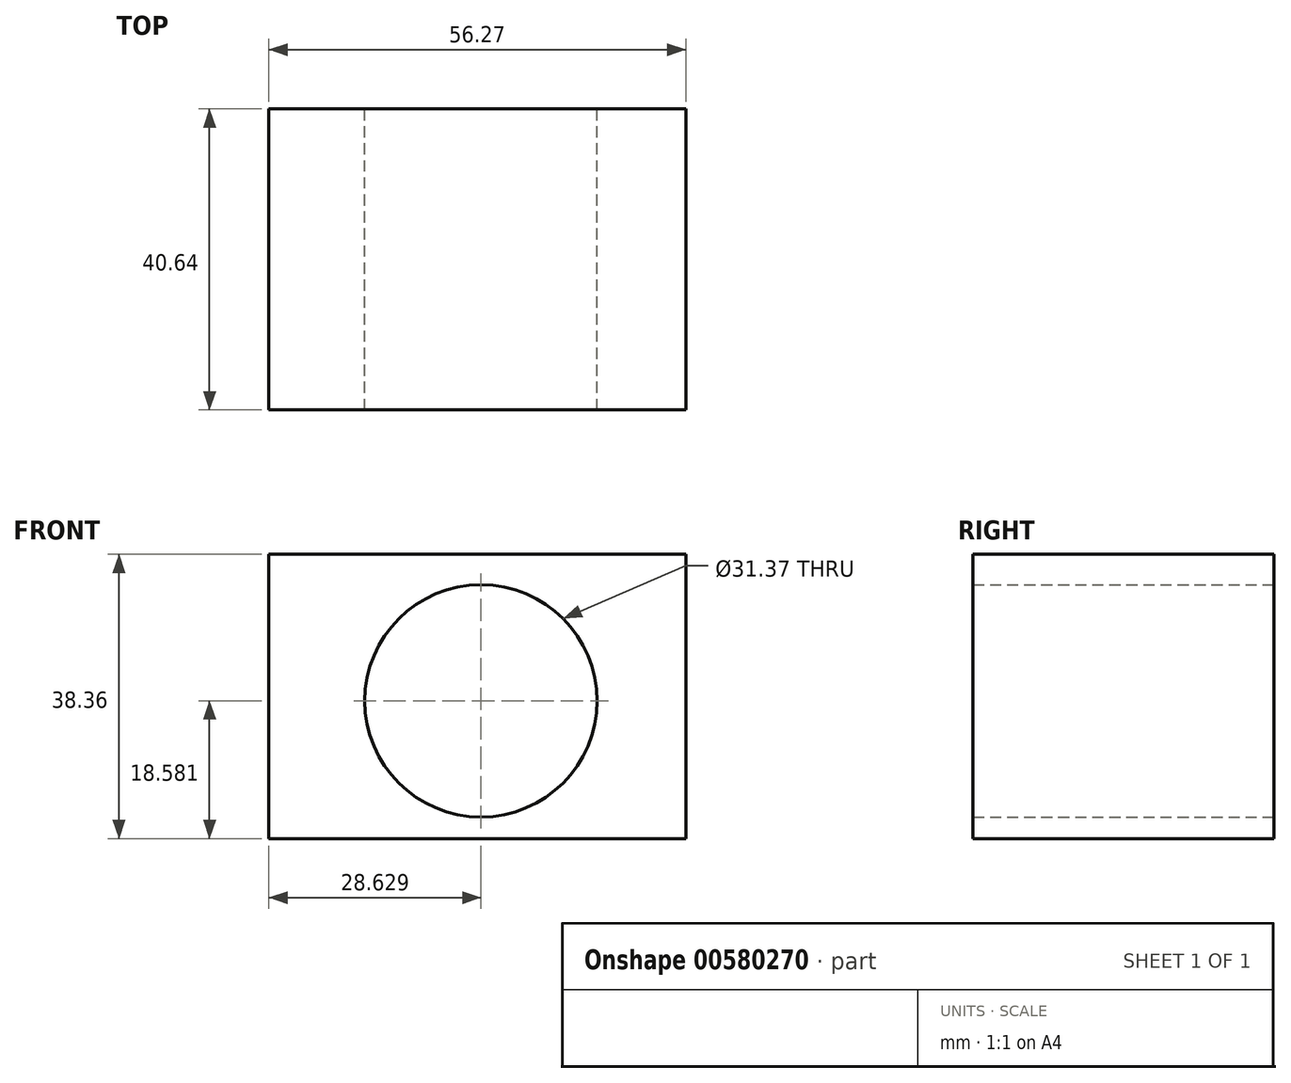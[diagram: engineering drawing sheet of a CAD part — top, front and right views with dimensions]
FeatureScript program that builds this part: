
annotation { "Feature Type Name" : "Feature", "Feature Type Description" : "" }
export const myFeature = defineFeature(function(context is Context, id is Id, definition is map)
    precondition{}
    {
        {
            var Q0;
            Q0=qCreatedBy(makeId("Front.planeOp"),FACE);
            var sketch = newSketch(context, id + "F0", { "sketchPlane" : qUnion([Q0])});
            skLineSegment(sketch, "E0.bottom", {"start": v(0, 0) * mm, "end": v(56.27, 0) * mm});
            skLineSegment(sketch, "E0.top", {"start": v(0, 38.36) * mm, "end": v(56.27, 38.36) * mm});
            skLineSegment(sketch, "E0.left", {"start": v(0, 0) * mm, "end": v(0, 38.36) * mm});
            skLineSegment(sketch, "E0.right", {"start": v(56.27, 0) * mm, "end": v(56.27, 38.36) * mm});
            skSolve(sketch);
        }
        {
            var Q0;
            Q0 = qSketchRegion(id + "F0", true);
            extrude(context, id + "F1", {"entities" : qUnion([Q0]), "depth" : 40.64 * mm, "offsetDistance" : 25.4 * mm});
        }
        {
            var Q0;
            Q0=qCreatedBy(makeId("Front.planeOp"),FACE);
            var sketch = newSketch(context, id + "F2", { "sketchPlane" : qUnion([Q0])});
            skCircle(sketch, "E1", {"center": v(28.63, 18.58) * mm, "radius": 15.69 * mm});
            skSolve(sketch);
        }
        {
            var Q0;
            Q0 = qSketchRegion(id + "F2", true);
            extrude(context, id + "F3", {"entities" : qUnion([Q0]), "operationType" : NewBodyOperationType.REMOVE, "endBound" : BoundingType.THROUGH_ALL, "depth" : 41.15 * mm, "offsetDistance" : 25.4 * mm});
        }
    });
